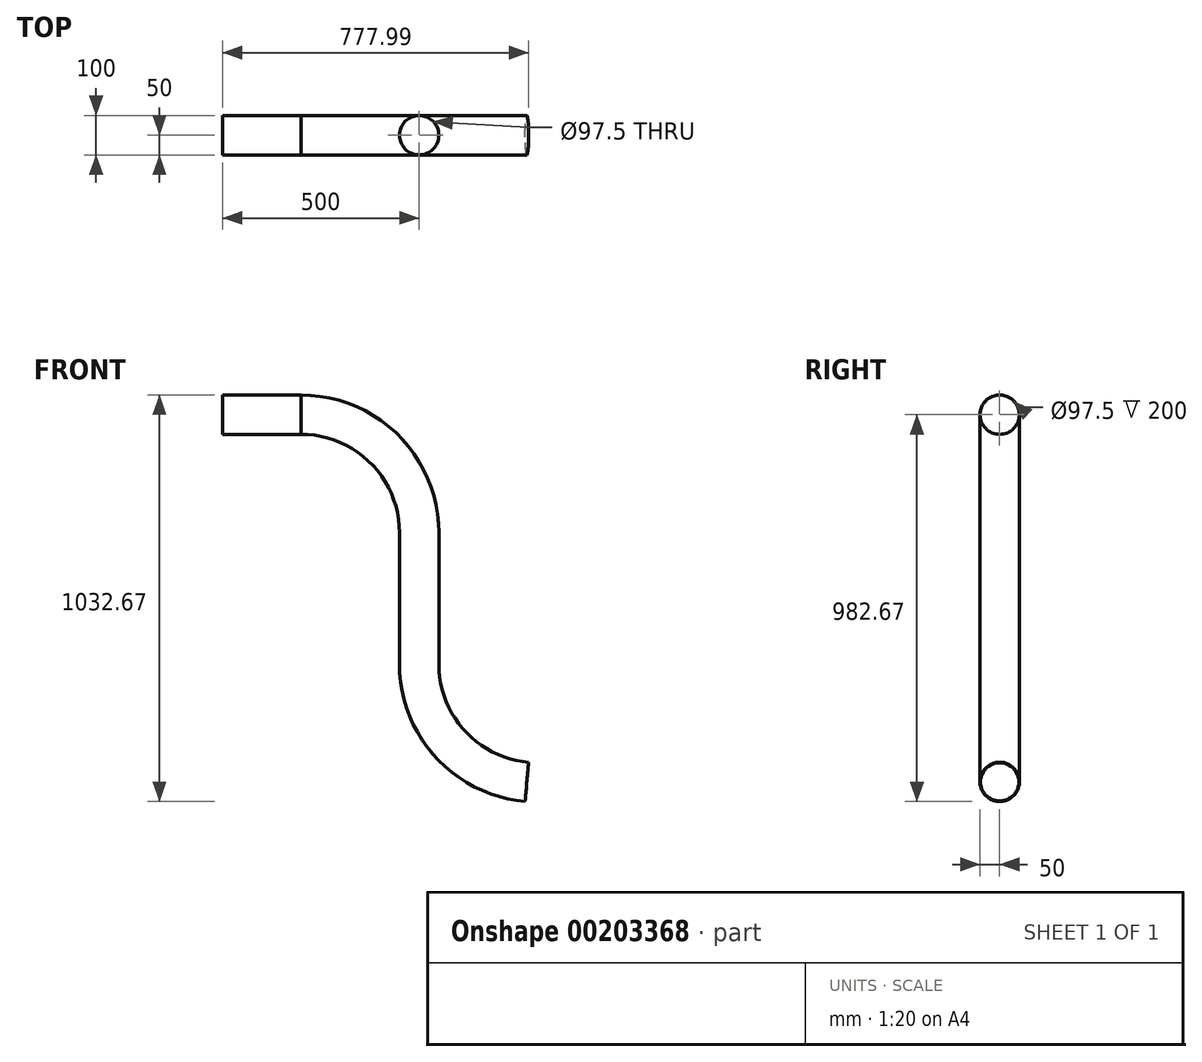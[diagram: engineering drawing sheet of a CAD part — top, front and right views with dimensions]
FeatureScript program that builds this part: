
annotation { "Feature Type Name" : "Feature", "Feature Type Description" : "" }
export const myFeature = defineFeature(function(context is Context, id is Id, definition is map)
    precondition{}
    {
        {
            var Q0;
            Q0=qCreatedBy(makeId("Front.planeOp"),FACE);
            var sketch = newSketch(context, id + "F5", { "sketchPlane" : qUnion([Q0])});
            skLineSegment(sketch, "E0", {"start": v(0, 60) * mm, "end": v(200, 60) * mm});
            skArc(sketch, "E1", {"start": v(200, 60) * mm, "mid": v(412.13, -27.87) * mm, "end": v(500, -240) * mm});
            skLineSegment(sketch, "E2", {"start": v(500, -240) * mm, "end": v(500, -574.03) * mm});
            skArc(sketch, "E3", {"start": v(500, -574.03) * mm, "mid": v(578.73, -776.6) * mm, "end": v(773.59, -872.87) * mm});
            skSolve(sketch);
        }
        {
            var Q0;
            Q0=sQuery(id+"F5.wireOp",VERTEX,"E0.start");
            var Q1;
            Q1=sQuery(id+"F5.wireOp",EDGE,"E0");
            cPlane(context, id + "F0", {"entities" : qUnion([Q0, Q1]), "cplaneType" : CPlaneType.CURVE_POINT, "offset" : 25 * mm, "width" : 150 * mm, "height" : 150 * mm});
        }
        {
            var Q0;
            Q0=qCreatedBy(id+"F0.planeOp",FACE);
            var sketch = newSketch(context, id + "F1", { "sketchPlane" : qUnion([Q0])});
            skCircle(sketch, "E4", {"center": v(0, 60) * mm, "radius": 50 * mm});
            skCircle(sketch, "E5", {"center": v(0, 60) * mm, "radius": 48.75 * mm});
            skSolve(sketch);
        }
        {
            var Q0;
            Q0=makeQuery(id+"F1.imprint","IMPRINT",FACE,{"disambiguationData":[TD([[makeQuery(id+"F1.imprint","IMPRINT",EDGE,{"derivedFrom":sQuery(id+"F1.wireOp",EDGE,"E4")}),1.0]])]});
            var Q1;
            Q1=sQuery(id+"F5.wireOp",EDGE,"E0");
            sweep(context, id + "F2", {"profiles" : qUnion([Q0]), "path" : qUnion([Q1])});
        }
        {
            var Q0;
            Q0=makeQuery(id+"F2.opSweep","CAP_FACE",FACE,{"disambiguationData":[OSD([sQuery(id+"F5.wireOp",VERTEX,"E0.end"),sQuery(id+"FkulyD3NrFC+YYhx0_0.wireOp",EDGE,"a7676385-1627-4b60-94bb-6bd7cbd8406d"),sQuery(id+"FkulyD3NrFC+YYhx0_0.wireOp",EDGE,"8eb30a48-0cbe-466f-a34e-f4396f98498a")])],"isStart":false});
            var Q1;
            Q1=sQuery(id+"F5.wireOp",EDGE,"E1");
            sweep(context, id + "F6", {"profiles" : qUnion([Q0]), "path" : qUnion([Q1])});
        }
        {
            var Q0;
            Q0=makeQuery(id+"F6.opSweep","CAP_FACE",FACE,{"disambiguationData":[OSD([sQuery(id+"F5.wireOp",VERTEX,"E0.end"),sQuery(id+"F5.wireOp",VERTEX,"E1.end"),sQuery(id+"FkulyD3NrFC+YYhx0_0.wireOp",EDGE,"a7676385-1627-4b60-94bb-6bd7cbd8406d"),sQuery(id+"FkulyD3NrFC+YYhx0_0.wireOp",EDGE,"8eb30a48-0cbe-466f-a34e-f4396f98498a")])],"isStart":false});
            var Q1;
            Q1=sQuery(id+"F5.wireOp",EDGE,"E2");
            sweep(context, id + "F3", {"operationType" : NewBodyOperationType.ADD, "profiles" : qUnion([Q0]), "path" : qUnion([Q1])});
        }
        {
            var Q0;
            Q0=makeQuery(id+"F3.opSweep","CAP_FACE",FACE,{"disambiguationData":[OSD([sQuery(id+"F5.wireOp",VERTEX,"E0.end"),sQuery(id+"F5.wireOp",VERTEX,"E1.end"),sQuery(id+"F5.wireOp",VERTEX,"E2.end"),sQuery(id+"FkulyD3NrFC+YYhx0_0.wireOp",EDGE,"a7676385-1627-4b60-94bb-6bd7cbd8406d"),sQuery(id+"FkulyD3NrFC+YYhx0_0.wireOp",EDGE,"8eb30a48-0cbe-466f-a34e-f4396f98498a")])],"isStart":false});
            var Q1;
            Q1=sQuery(id+"F5.wireOp",EDGE,"E3");
            sweep(context, id + "F4", {"operationType" : NewBodyOperationType.ADD, "profiles" : qUnion([Q0]), "path" : qUnion([Q1])});
        }
    });
